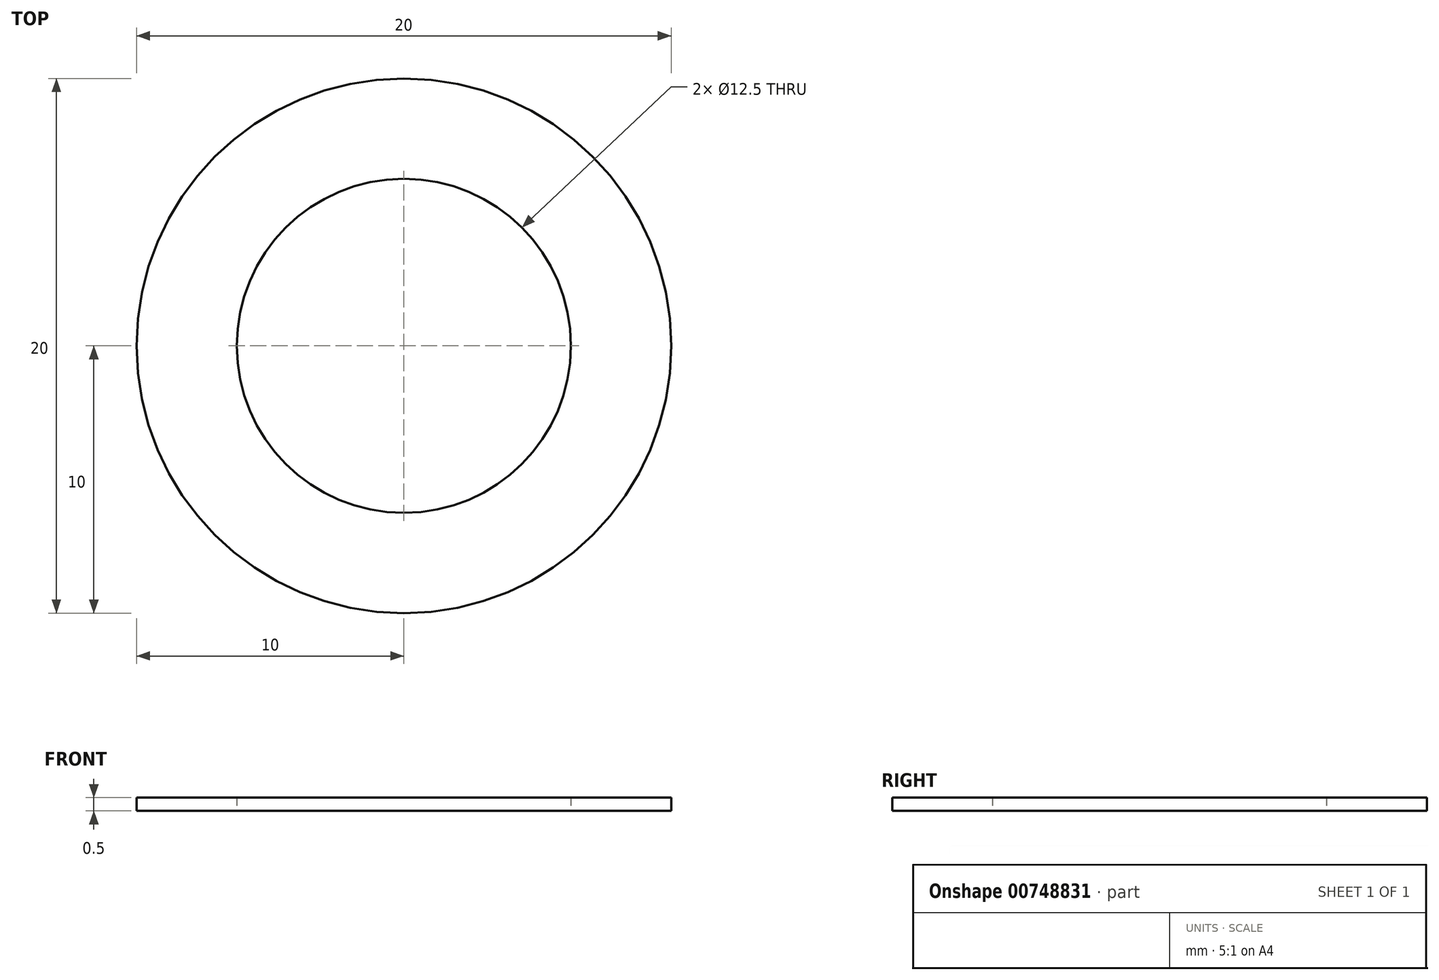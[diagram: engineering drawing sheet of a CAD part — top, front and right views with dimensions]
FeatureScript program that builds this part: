
annotation { "Feature Type Name" : "Feature", "Feature Type Description" : "" }
export const myFeature = defineFeature(function(context is Context, id is Id, definition is map)
    precondition{}
    {
        {
            var Q0;
            Q0=qCreatedBy(makeId("Top.planeOp"),FACE);
            var sketch = newSketch(context, id + "F0", { "sketchPlane" : qUnion([Q0])});
            skCircle(sketch, "E0", {"center": v(0, 0) * mm, "radius": 10 * mm});
            skCircle(sketch, "E1", {"center": v(0, 0) * mm, "radius": 6.25 * mm});
            skSolve(sketch);
        }
        {
            var Q0;
            Q0 = qSketchRegion(id + "F0", true);
            extrude(context, id + "F1", {"entities" : qUnion([Q0]), "depth" : 0.5 * mm, "offsetDistance" : 25 * mm});
        }
    });
